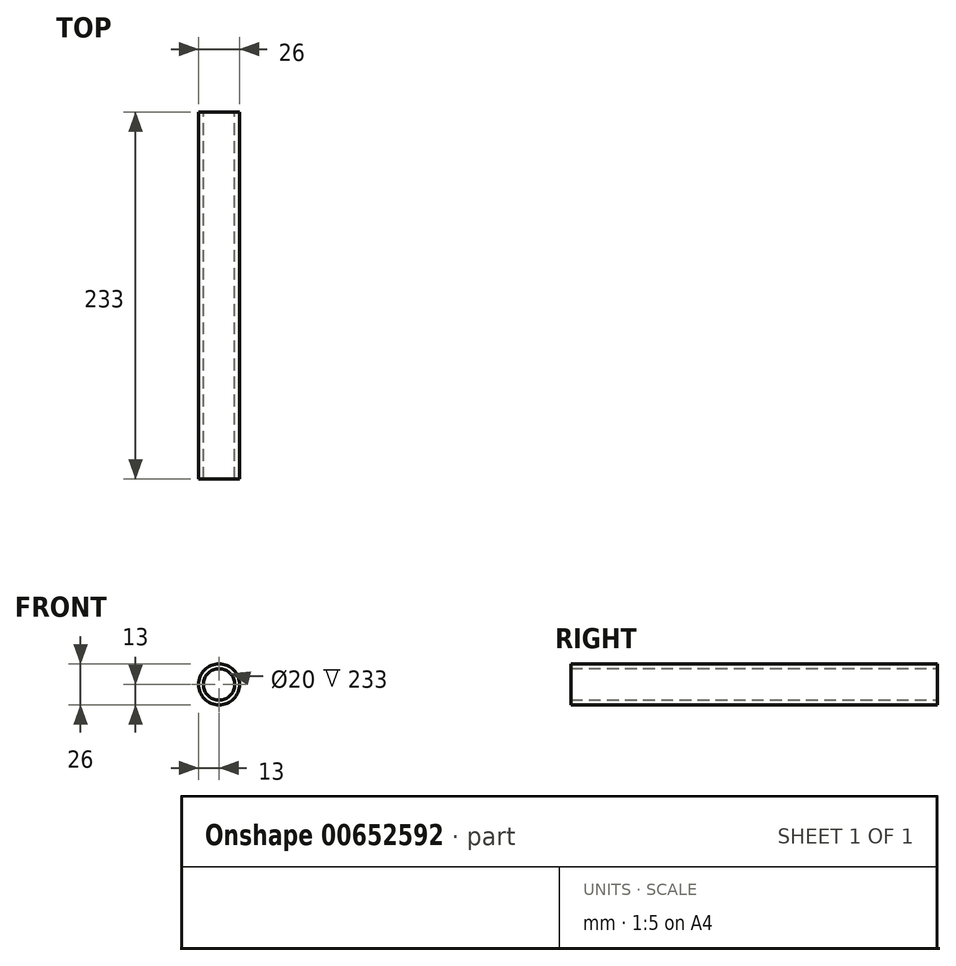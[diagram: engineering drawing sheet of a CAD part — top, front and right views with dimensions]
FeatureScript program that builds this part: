
annotation { "Feature Type Name" : "Feature", "Feature Type Description" : "" }
export const myFeature = defineFeature(function(context is Context, id is Id, definition is map)
    precondition{}
    {
        {
            var Q0;
            Q0=qCreatedBy(makeId("Front.planeOp"),FACE);
            var sketch = newSketch(context, id + "F0", { "sketchPlane" : qUnion([Q0])});
            skCircle(sketch, "E0", {"center": v(0, 0) * mm, "radius": 10 * mm});
            skCircle(sketch, "E1", {"center": v(0, 0) * mm, "radius": 13 * mm});
            skSolve(sketch);
        }
        {
            var Q0;
            Q0 = qSketchRegion(id + "F0", true);
            extrude(context, id + "F1", {"entities" : qUnion([Q0]), "depth" : (200 + 33) * mm, "offsetDistance" : 25 * mm});
        }
    });
